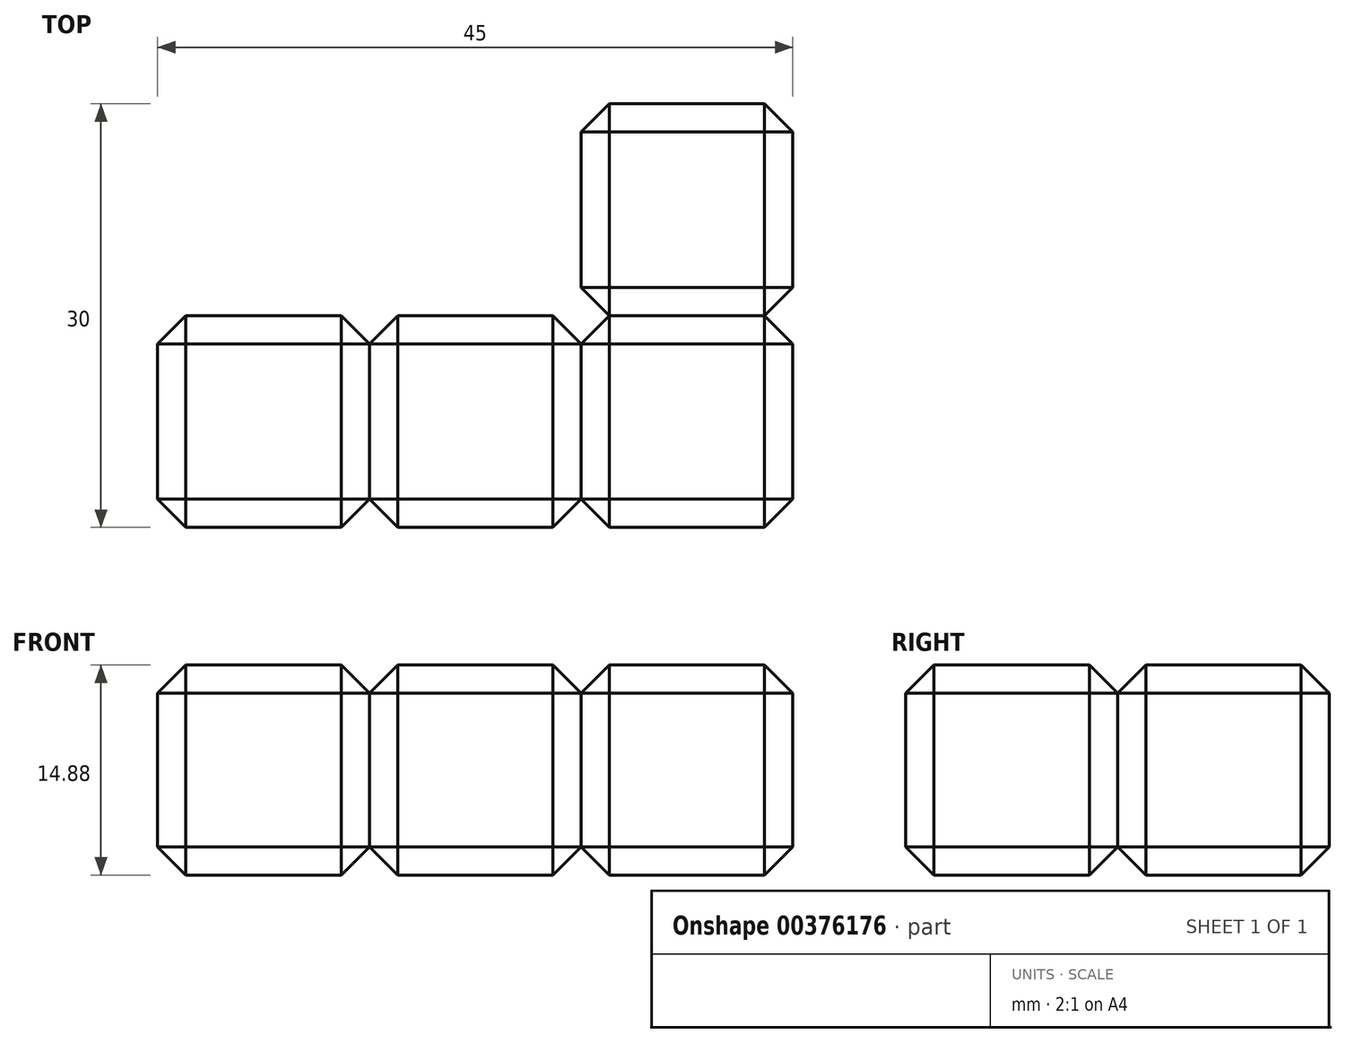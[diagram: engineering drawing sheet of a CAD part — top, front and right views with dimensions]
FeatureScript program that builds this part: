
annotation { "Feature Type Name" : "Feature", "Feature Type Description" : "" }
export const myFeature = defineFeature(function(context is Context, id is Id, definition is map)
    precondition{}
    {
        {
            var Q0;
            Q0=qCreatedBy(makeId("Front.planeOp"),FACE);
            var sketch = newSketch(context, id + "F0", { "sketchPlane" : qUnion([Q0])});
            skLineSegment(sketch, "E0.bottom", {"start": v(7.5, -7.44) * mm, "end": v(-7.5, -7.44) * mm});
            skLineSegment(sketch, "E0.top", {"start": v(7.5, 7.44) * mm, "end": v(-7.5, 7.44) * mm});
            skLineSegment(sketch, "E0.left", {"start": v(7.5, -7.44) * mm, "end": v(7.5, 7.44) * mm});
            skLineSegment(sketch, "E0.right", {"start": v(-7.5, -7.44) * mm, "end": v(-7.5, 7.44) * mm});
            skPoint(sketch, "E0.middle", {"position": v(0, 0) * mm});
            skSolve(sketch);
        }
        {
            var Q0;
            Q0 = qSketchRegion(id + "F0", true);
            extrude(context, id + "F1", {"entities" : qUnion([Q0]), "depth" : 15 * mm});
        }
        {
            var Q0;
            Q0=makeQuery(id+"F1.opExtrude","SWEPT_FACE",FACE,{"disambiguationData":[OSD([sQuery(id+"F0.wireOp",EDGE,"E0.top")])]});
            var Q1;
            Q1=makeQuery(id+"F1.opExtrude","CAP_FACE",FACE,{"disambiguationData":[OSD([sQuery(id+"F0.wireOp",EDGE,"E0.bottom"),sQuery(id+"F0.wireOp",EDGE,"E0.top"),sQuery(id+"F0.wireOp",EDGE,"E0.left"),sQuery(id+"F0.wireOp",EDGE,"E0.right")])],"isStart":false});
            var Q2;
            Q2=makeQuery(id+"F1.opExtrude","SWEPT_FACE",FACE,{"disambiguationData":[OSD([sQuery(id+"F0.wireOp",EDGE,"E0.right")])]});
            var Q3;
            Q3=makeQuery(id+"F1.opExtrude","CAP_FACE",FACE,{"disambiguationData":[OSD([sQuery(id+"F0.wireOp",EDGE,"E0.bottom"),sQuery(id+"F0.wireOp",EDGE,"E0.top"),sQuery(id+"F0.wireOp",EDGE,"E0.left"),sQuery(id+"F0.wireOp",EDGE,"E0.right")])],"isStart":true});
            var Q4;
            Q4=makeQuery(id+"F1.opExtrude","SWEPT_FACE",FACE,{"disambiguationData":[OSD([sQuery(id+"F0.wireOp",EDGE,"E0.left")])]});
            chamfer(context, id + "F2", {"entities" : qUnion([Q0, Q1, Q2, Q3, Q4]), "width" : 2 * mm, "tangentPropagation" : true});
        }
        {
            var Q0;
            Q0=makeQuery(id+"F1.opExtrude","SWEPT_BODY",BODY,{"disambiguationData":[OSD([sQuery(id+"F0.wireOp",EDGE,"E0.bottom"),sQuery(id+"F0.wireOp",EDGE,"E0.top"),sQuery(id+"F0.wireOp",EDGE,"E0.left"),sQuery(id+"F0.wireOp",EDGE,"E0.right")])]});
            transform(context, id + "F3", {"entities" : qUnion([Q0]), "transformType" : TransformType.TRANSLATION_3D, "dx" : 15 * mm, "dy" : 0 * mm, "dz" : 0 * mm, "makeCopy" : true});
        }
        {
            var Q0;
            Q0=makeQuery(id+"F3.opPattern","COPY",BODY,{"derivedFrom":makeQuery(id+"F1.opExtrude","SWEPT_BODY",BODY,{"disambiguationData":[OSD([sQuery(id+"F0.wireOp",EDGE,"E0.bottom"),sQuery(id+"F0.wireOp",EDGE,"E0.top"),sQuery(id+"F0.wireOp",EDGE,"E0.left"),sQuery(id+"F0.wireOp",EDGE,"E0.right")])]}),"instanceName":"1"});
            transform(context, id + "F4", {"entities" : qUnion([Q0]), "transformType" : TransformType.TRANSLATION_3D, "dx" : 15 * mm, "dy" : 0 * mm, "dz" : 0 * mm, "makeCopy" : true});
        }
        {
            var Q0;
            Q0=makeQuery(id+"F4.opPattern","COPY",BODY,{"derivedFrom":makeQuery(id+"F3.opPattern","COPY",BODY,{"derivedFrom":makeQuery(id+"F1.opExtrude","SWEPT_BODY",BODY,{"disambiguationData":[OSD([sQuery(id+"F0.wireOp",EDGE,"E0.bottom"),sQuery(id+"F0.wireOp",EDGE,"E0.top"),sQuery(id+"F0.wireOp",EDGE,"E0.left"),sQuery(id+"F0.wireOp",EDGE,"E0.right")])]}),"instanceName":"1"}),"instanceName":"1"});
            transform(context, id + "F5", {"entities" : qUnion([Q0]), "transformType" : TransformType.TRANSLATION_3D, "dx" : 0 * mm, "dy" : 15 * mm, "dz" : 0 * mm, "makeCopy" : true});
        }
    });
